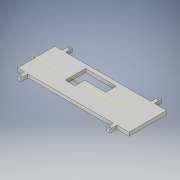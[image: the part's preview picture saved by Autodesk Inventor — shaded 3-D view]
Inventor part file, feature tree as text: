
AUTODESK INVENTOR PART (.ipt)
format: ipt  version: 2018 (Build 220112000, 112)  size: 154,112 bytes
history: native  units: in
note: dims shown in document units (in); Inventor stores cm internally (conversion verified against a paired STEP export)
features: extrude x3, sketch x3, plane x1, mirror x1
ambient origin geometry x8: Origin, YZ Plane, XZ Plane, XY Plane, X Axis, Y Axis, Z Axis, Center Point
bodies: Solid1 (feature_tree)
feature tree (8):
  extrude  "Extrusion1"  Depth=2.7in
  extrude  "Extrusion2"  TaperAngle=0.0deg  [1 undecoded]
  plane  "Work Plane1"
  mirror  "Mirror1"
  extrude  "Extrusion3"  Depth=0.5in
  sketch  "Sketch1"  dims[d0=8.0in d1=2.7in]
  sketch  "Sketch2"  dims[d2=0.25in d3=0.0in]
  sketch  "Sketch3"  dims[d4=0.5in d5=0.25in d6=0.11in d7=0.125in d8=0.125in d9=0.0in d10=0.5in d11=0.5in d12=0.25in d13=0.11in d14=0.125in d15=0.125in d16=0.0in d18=0.25in d19=0.0in d20=1.0in d21=0.75in d22=2.2in d23=0.7in d24=0.7in d25=0.3in d26=1.0in d27=0.0in]
note: 1 required parameter value undecoded (feature->parameter linkage not recoverable at this tier; creation-order binding heuristic only, values carry confidence <= 0.55)
